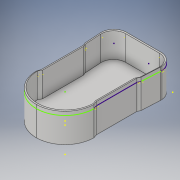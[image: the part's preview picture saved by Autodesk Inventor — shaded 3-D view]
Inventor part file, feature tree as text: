
AUTODESK INVENTOR PART (.ipt)
format: ipt  version: 2018 (Build 220112000, 112)  size: 184,320 bytes
history: native  units: in
note: dims shown in document units (in); Inventor stores cm internally (conversion verified against a paired STEP export)
features: sketch x10, extrude x2, plane x1
ambient origin geometry x8: Origin, YZ Plane, XZ Plane, XY Plane, X Axis, Y Axis, Z Axis, Center Point
bodies: Solid1 (feature_tree)
feature tree (13):
  sketch  "Sketch1"  dims[d2=1.162in d3=0.0in d5=1.1591in]
  extrude  "Extrusion1"  Depth=1.1591in
  extrude  "Extrusion2"  Depth=0.8in
  sketch  "Sketch4"  dims[d9=1.124in d10=1.5753in d11=0.776in d12=0.485in]
  sketch  "Sketch5"  dims[d13=1.0in d14=0.0in]
  sketch  "3D Sketch1"
  sketch  "3D Sketch2"
  sketch  "3D Sketch3"
  sketch  "Sketch6"
  plane  "Work Plane3"
  sketch  "Sketch7"
  sketch  "Sketch2"  dims[d6=1.624in d7=0.8in]
  sketch  "Sketch3"  dims[d8=0.5in]
